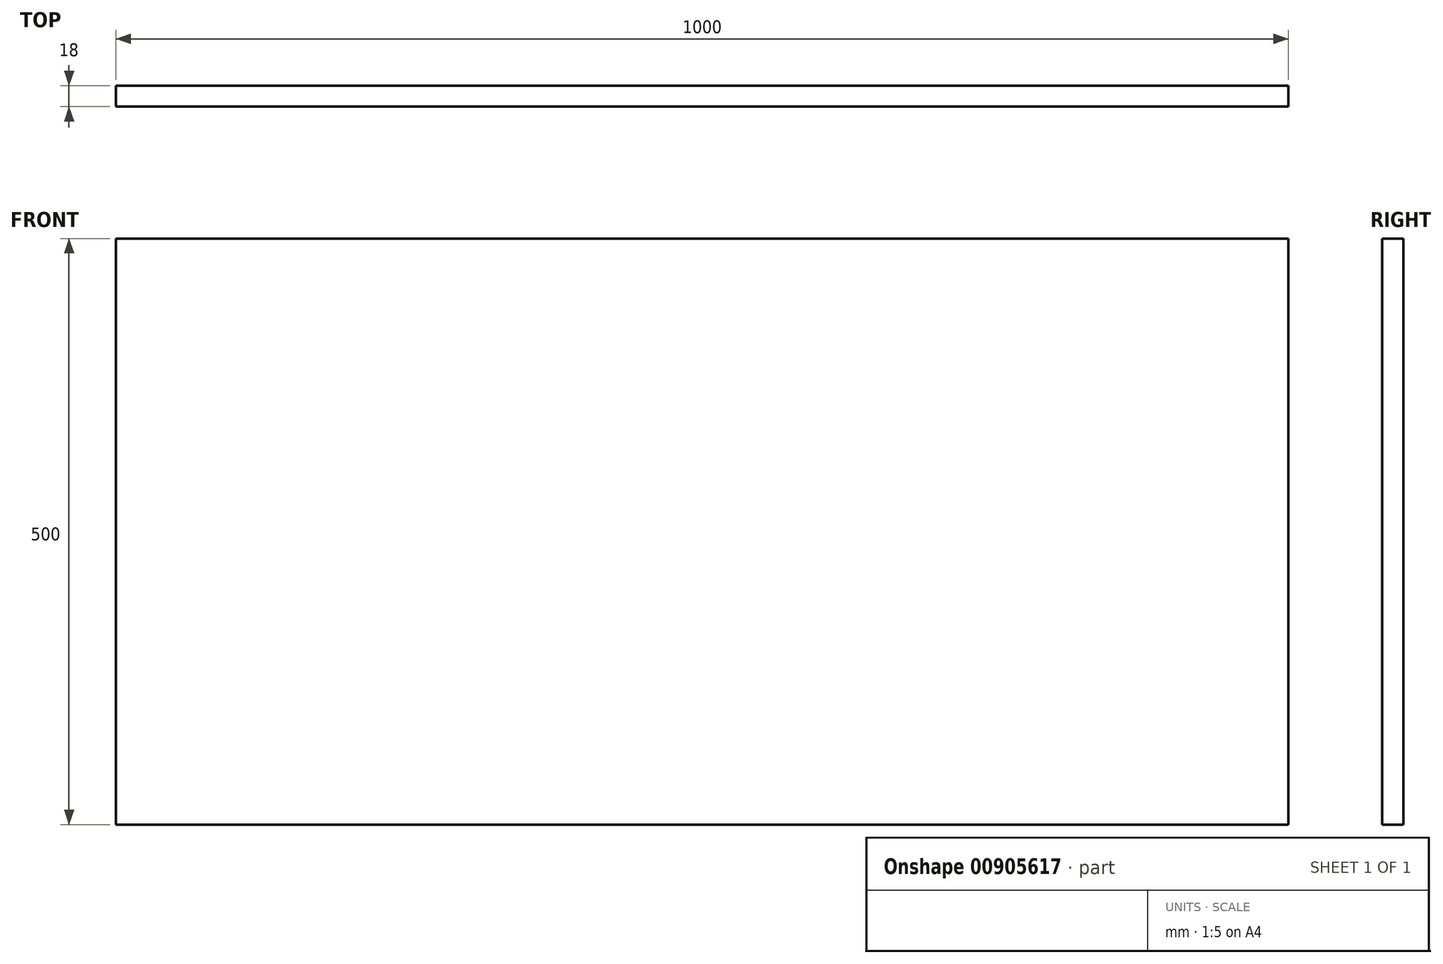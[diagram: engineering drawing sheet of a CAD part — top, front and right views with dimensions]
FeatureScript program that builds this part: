
annotation { "Feature Type Name" : "Feature", "Feature Type Description" : "" }
export const myFeature = defineFeature(function(context is Context, id is Id, definition is map)
    precondition{}
    {
        {
            var Q0;
            Q0=qCreatedBy(makeId("Front.planeOp"),FACE);
            var sketch = newSketch(context, id + "F0", { "sketchPlane" : qUnion([Q0])});
            skLineSegment(sketch, "E0.bottom", {"start": v(500, 250) * mm, "end": v(-500, 250) * mm});
            skLineSegment(sketch, "E0.top", {"start": v(500, -250) * mm, "end": v(-500, -250) * mm});
            skLineSegment(sketch, "E0.left", {"start": v(500, 250) * mm, "end": v(500, -250) * mm});
            skLineSegment(sketch, "E0.right", {"start": v(-500, 250) * mm, "end": v(-500, -250) * mm});
            skPoint(sketch, "E0.middle", {"position": v(0, 0) * mm});
            skSolve(sketch);
        }
        {
            var Q0;
            Q0=makeQuery(id+"F0.imprint","IMPRINT",FACE,{"disambiguationData":[TD([[makeQuery(id+"F0.imprint","IMPRINT",EDGE,{"derivedFrom":sQuery(id+"F0.wireOp",EDGE,"E0.bottom")}),1.0]])]});
            extrude(context, id + "F1", {"entities" : qUnion([Q0]), "depth" : 18 * mm, "offsetDistance" : 25 * mm});
        }
    });
